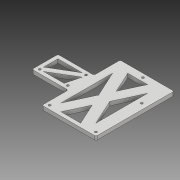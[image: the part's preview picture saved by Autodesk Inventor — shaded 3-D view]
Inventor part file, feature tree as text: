
AUTODESK INVENTOR PART (.ipt)
format: ipt  version: 2018 (Build 220112000, 112)  size: 241,664 bytes
history: native  units: mm
features: extrude x5, sketch x5, fillet x2, other x1
ambient origin geometry x8: Origin, YZ Plane, XZ Plane, XY Plane, X Axis, Y Axis, Z Axis, Center Point
bodies: Body1 (feature_tree)
feature tree (13):
  other  "Sólido1"
  extrude  "Extrusión1"  Depth=3.0mm
  extrude  "Extrusión2"  Depth=3.0mm
  extrude  "Extrusión3"  Depth=61.0mm
  fillet  "Empalme1"  Radius=3.0mm
  fillet  "Empalme2"  Radius=61.0mm
  extrude  "Extrusión4"  Depth=5.0mm
  extrude  "Extrusión5"  Depth=5.0mm
  sketch  "Boceto1"  dims[d0=3.0mm d1=28.5mm]
  sketch  "Boceto2"  dims[d2=30.0mm d3=3.0mm]
  sketch  "Boceto3"  dims[d4=63.0mm d5=2.5mm d6=3.0mm d7=61.0mm]
  sketch  "Boceto4"  dims[d8=3.0mm d9=5.0mm]
  sketch  "Boceto5"  dims[d10=5.0mm d11=5.0mm d12=5.0mm d15=12.0mm d16=12.0mm d17=3.0mm d18=3.0mm d19=37.0mm d20=3.0mm d21=5.0mm d22=5.0mm d23=5.0mm d26=5.0mm d27=0.0mm d28=6.0mm d29=6.0mm d30=6.0mm d31=6.0mm d32=6.0mm d33=6.0mm d34=3.0mm d35=0.0mm d36=7.5mm d37=5.0mm d38=5.0mm d39=5.0mm d40=5.0mm d41=5.0mm d42=5.0mm d43=5.0mm d44=0.0mm d45=2.0mm d46=2.0mm d47=5.0mm d48=0.0mm d49=10.0mm d50=10.0mm d51=10.0mm d52=10.0mm d53=10.0mm d54=10.0mm d55=10.0mm d56=10.0mm d57=5.0mm d58=0.0mm]
